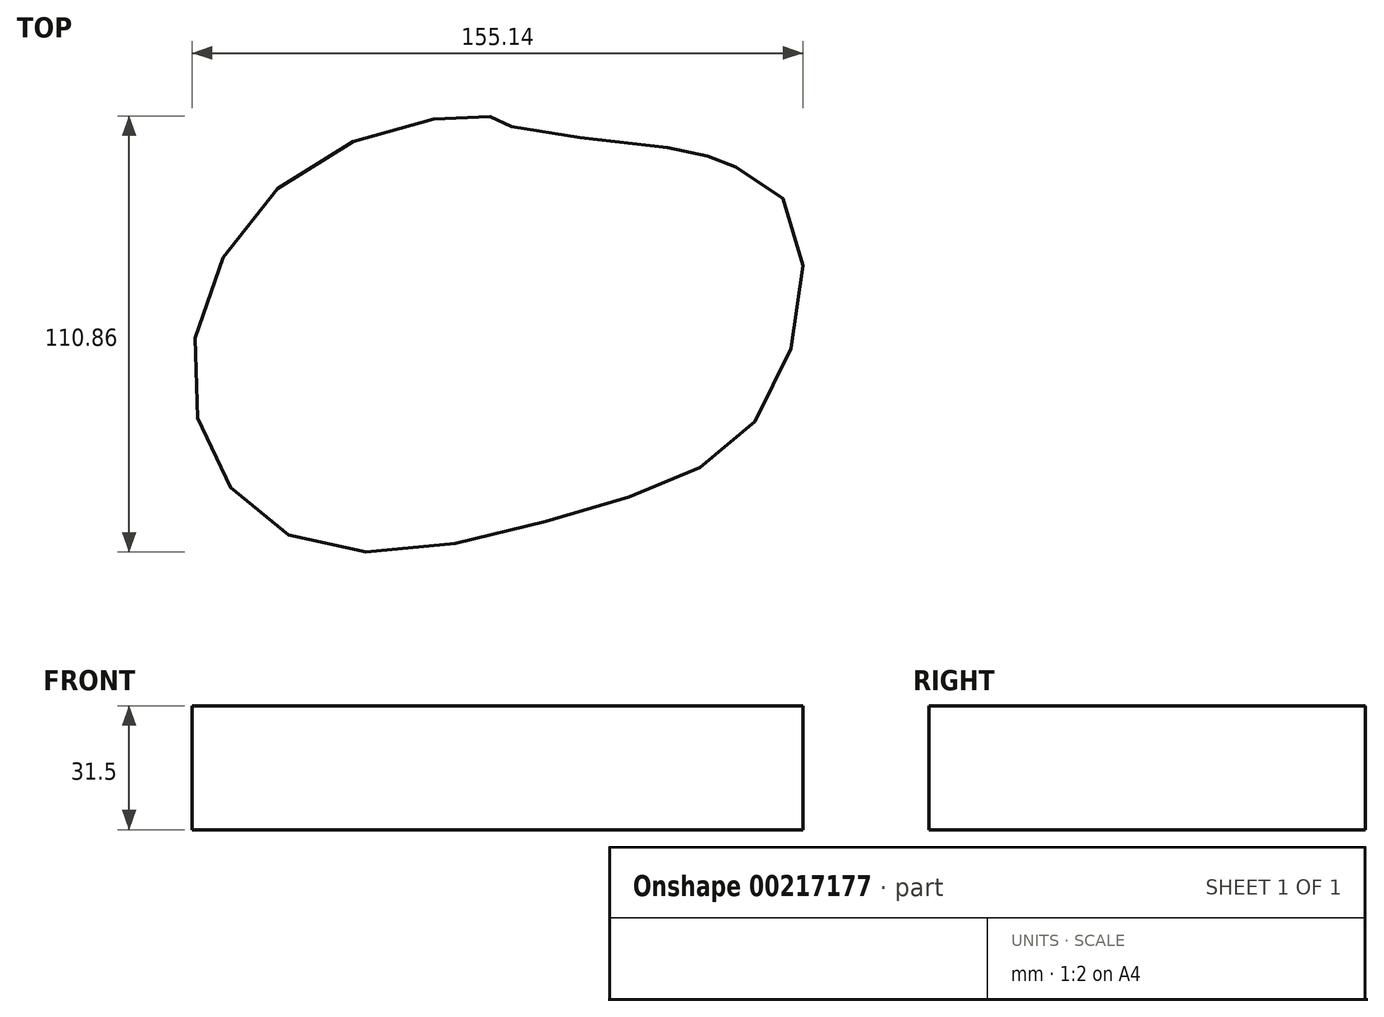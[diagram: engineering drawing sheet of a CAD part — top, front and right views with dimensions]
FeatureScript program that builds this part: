
annotation { "Feature Type Name" : "Feature", "Feature Type Description" : "" }
export const myFeature = defineFeature(function(context is Context, id is Id, definition is map)
    precondition{}
    {
        {
            var Q0;
            Q0=qCreatedBy(makeId("Top.planeOp"),FACE);
            var sketch = newSketch(context, id + "F0", { "sketchPlane" : qUnion([Q0])});
            skFitSpline(sketch, "E0", {"points": [v(68.93, 31.29) * mm, v(64.04, -22.03) * mm, v(18.1, -48) * mm, v(-53.2, -55.69) * mm, v(-81.17, -14.52) * mm, v(-49.34, 41.43) * mm, v(-4.43, 51.86) * mm, v(0, 49.58) * mm, v(48.57, 42.76) * mm, v(50.38, 41.57) * mm, v(68.93, 31.29) * mm]});
            skSolve(sketch);
        }
        {
            var Q0;
            Q0 = qSketchRegion(id + "F0", true);
            extrude(context, id + "F1", {"entities" : qUnion([Q0]), "depth" : 31.5 * mm});
        }
    });
